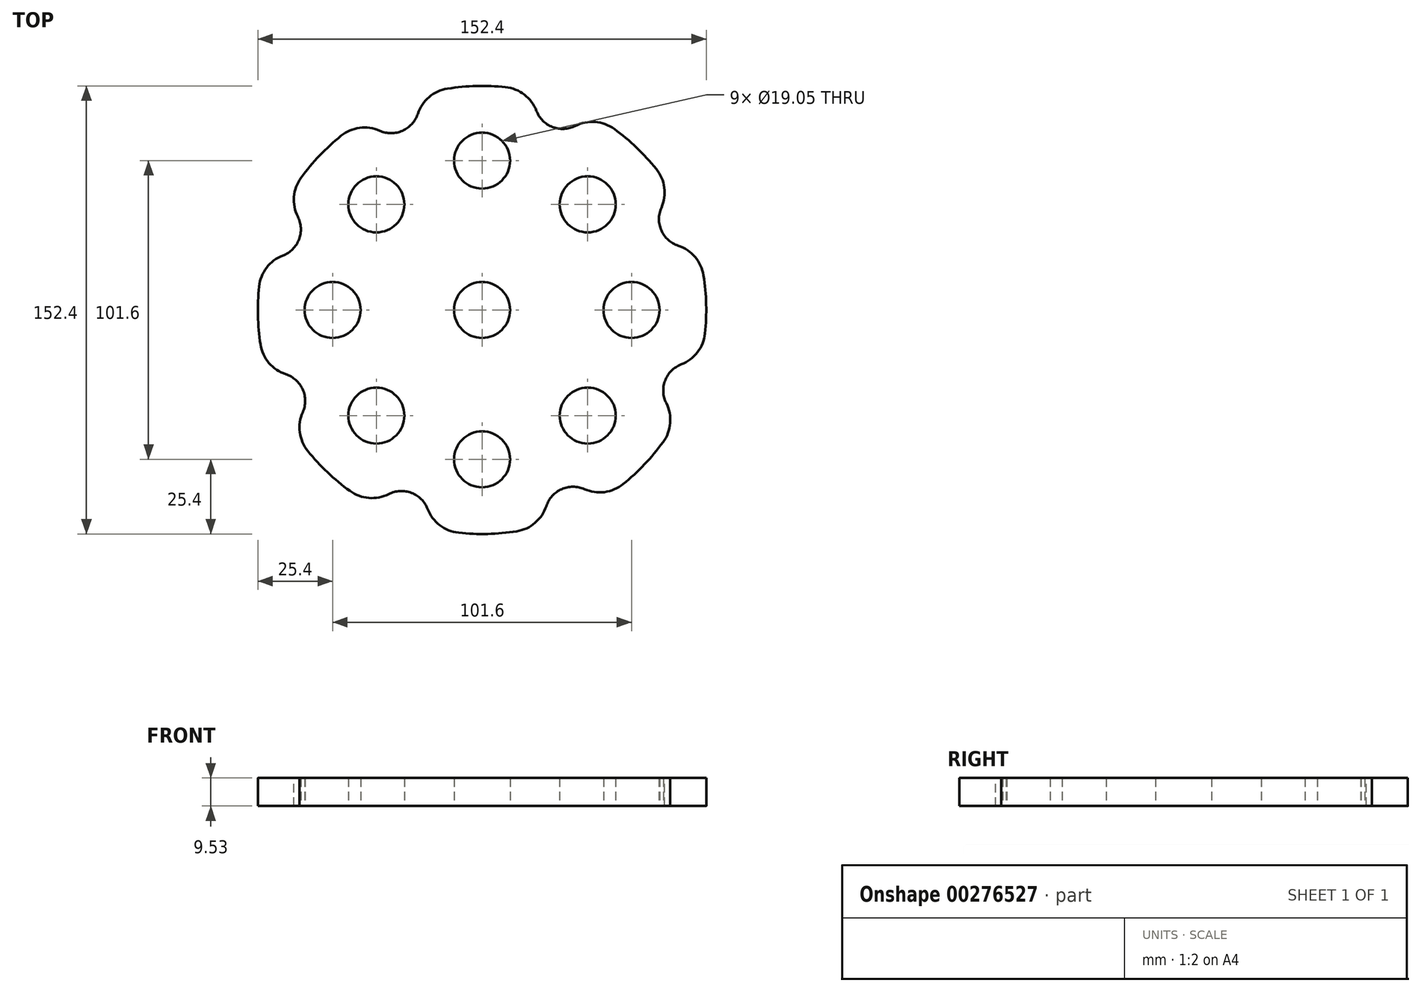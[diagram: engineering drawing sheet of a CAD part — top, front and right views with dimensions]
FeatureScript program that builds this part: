
annotation { "Feature Type Name" : "Feature", "Feature Type Description" : "" }
export const myFeature = defineFeature(function(context is Context, id is Id, definition is map)
    precondition{}
    {
        {
            var Q0;
            Q0=qCreatedBy(makeId("Top.planeOp"),FACE);
            var sketch = newSketch(context, id + "F0", { "sketchPlane" : qUnion([Q0])});
            skCircle(sketch, "E0", {"center": v(0, 0) * mm, "radius": 9.53 * mm});
            skCircle(sketch, "E1", {"center": v(0, 50.8) * mm, "radius": 9.53 * mm});
            skArc(sketch, "E2", {"start": v(-73.97, 18.31) * mm, "mid": v(-76.18, -1.9) * mm, "end": v(-72.96, -21.97) * mm});
            skCircle(sketch, "E3.1.0", {"center": v(-35.92, 35.92) * mm, "radius": 9.53 * mm});
            skCircle(sketch, "E3.2.0", {"center": v(-50.8, 0) * mm, "radius": 9.53 * mm});
            skCircle(sketch, "E3.3.0", {"center": v(-35.92, -35.92) * mm, "radius": 9.53 * mm});
            skCircle(sketch, "E3.4.0", {"center": v(0, -50.8) * mm, "radius": 9.53 * mm});
            skCircle(sketch, "E3.5.0", {"center": v(35.92, -35.92) * mm, "radius": 9.53 * mm});
            skCircle(sketch, "E3.6.0", {"center": v(50.8, 0) * mm, "radius": 9.53 * mm});
            skCircle(sketch, "E3.7.0", {"center": v(35.92, 35.92) * mm, "radius": 9.53 * mm});
            skArc(sketch, "E4", {"start": v(-39.35, 65.25) * mm, "mid": v(-27.04, 60.95) * mm, "end": v(-21.97, 72.96) * mm});
            skArc(sketch, "E5.1.0", {"start": v(-73.97, 18.31) * mm, "mid": v(-62.22, 23.97) * mm, "end": v(-67.13, 36.05) * mm});
            skArc(sketch, "E5.2.0", {"start": v(-65.25, -39.35) * mm, "mid": v(-60.95, -27.04) * mm, "end": v(-72.96, -21.97) * mm});
            skArc(sketch, "E5.3.0", {"start": v(-18.31, -73.97) * mm, "mid": v(-23.97, -62.22) * mm, "end": v(-36.05, -67.13) * mm});
            skArc(sketch, "E5.4.0", {"start": v(39.35, -65.25) * mm, "mid": v(27.04, -60.95) * mm, "end": v(21.97, -72.96) * mm});
            skArc(sketch, "E5.5.0", {"start": v(73.97, -18.31) * mm, "mid": v(62.22, -23.97) * mm, "end": v(67.13, -36.05) * mm});
            skArc(sketch, "E5.6.0", {"start": v(65.25, 39.35) * mm, "mid": v(60.95, 27.04) * mm, "end": v(72.96, 21.97) * mm});
            skArc(sketch, "E5.7.0", {"start": v(18.31, 73.97) * mm, "mid": v(23.97, 62.22) * mm, "end": v(36.05, 67.13) * mm});
            skArc(sketch, "E6.trimOffspring", {"start": v(-39.35, 65.25) * mm, "mid": v(-55.2, 52.52) * mm, "end": v(-67.13, 36.05) * mm});
            skArc(sketch, "E7.trimOffspring", {"start": v(65.25, 39.35) * mm, "mid": v(52.52, 55.2) * mm, "end": v(36.05, 67.13) * mm});
            skArc(sketch, "E8.trimOffspring", {"start": v(18.31, 73.97) * mm, "mid": v(-1.9, 76.18) * mm, "end": v(-21.97, 72.96) * mm});
            skArc(sketch, "E9.trimOffspring", {"start": v(73.97, -18.31) * mm, "mid": v(76.18, 1.9) * mm, "end": v(72.96, 21.97) * mm});
            skArc(sketch, "E10.trimOffspring", {"start": v(39.35, -65.25) * mm, "mid": v(55.2, -52.52) * mm, "end": v(67.13, -36.05) * mm});
            skArc(sketch, "E11.trimOffspring", {"start": v(-18.31, -73.97) * mm, "mid": v(1.9, -76.18) * mm, "end": v(21.97, -72.96) * mm});
            skArc(sketch, "E12.trimOffspring", {"start": v(-65.25, -39.35) * mm, "mid": v(-52.52, -55.2) * mm, "end": v(-36.05, -67.13) * mm});
            skSolve(sketch);
        }
        {
            var Q0;
            Q0 = qSketchRegion(id + "F0", true);
            extrude(context, id + "F1", {"entities" : qUnion([Q0]), "depth" : 9.52 * mm});
        }
        {
            var Q0;
            Q0=makeQuery(id+"F1.opExtrude","SWEPT_EDGE",EDGE,{"disambiguationData":[OSD([sQuery(id+"F0.wireOp",EDGE,"E4"),sQuery(id+"F0.wireOp",EDGE,"E8.trimOffspring")])]});
            var Q1;
            Q1=makeQuery(id+"F1.opExtrude","SWEPT_EDGE",EDGE,{"disambiguationData":[OSD([sQuery(id+"F0.wireOp",EDGE,"E4"),sQuery(id+"F0.wireOp",EDGE,"E6.trimOffspring")])]});
            var Q2;
            Q2=makeQuery(id+"F1.opExtrude","SWEPT_EDGE",EDGE,{"disambiguationData":[OSD([sQuery(id+"F0.wireOp",EDGE,"E5.1.0"),sQuery(id+"F0.wireOp",EDGE,"E6.trimOffspring")])]});
            var Q3;
            Q3=makeQuery(id+"F1.opExtrude","SWEPT_EDGE",EDGE,{"disambiguationData":[OSD([sQuery(id+"F0.wireOp",EDGE,"E2"),sQuery(id+"F0.wireOp",EDGE,"E5.1.0")])]});
            var Q4;
            Q4=makeQuery(id+"F1.opExtrude","SWEPT_EDGE",EDGE,{"disambiguationData":[OSD([sQuery(id+"F0.wireOp",EDGE,"E2"),sQuery(id+"F0.wireOp",EDGE,"E5.2.0")])]});
            var Q5;
            Q5=makeQuery(id+"F1.opExtrude","SWEPT_EDGE",EDGE,{"disambiguationData":[OSD([sQuery(id+"F0.wireOp",EDGE,"E5.2.0"),sQuery(id+"F0.wireOp",EDGE,"E12.trimOffspring")])]});
            var Q6;
            Q6=makeQuery(id+"F1.opExtrude","SWEPT_EDGE",EDGE,{"disambiguationData":[OSD([sQuery(id+"F0.wireOp",EDGE,"E5.3.0"),sQuery(id+"F0.wireOp",EDGE,"E12.trimOffspring")])]});
            var Q7;
            Q7=makeQuery(id+"F1.opExtrude","SWEPT_EDGE",EDGE,{"disambiguationData":[OSD([sQuery(id+"F0.wireOp",EDGE,"E5.3.0"),sQuery(id+"F0.wireOp",EDGE,"E11.trimOffspring")])]});
            var Q8;
            Q8=makeQuery(id+"F1.opExtrude","SWEPT_EDGE",EDGE,{"disambiguationData":[OSD([sQuery(id+"F0.wireOp",EDGE,"E5.4.0"),sQuery(id+"F0.wireOp",EDGE,"E10.trimOffspring")])]});
            var Q9;
            Q9=makeQuery(id+"F1.opExtrude","SWEPT_EDGE",EDGE,{"disambiguationData":[OSD([sQuery(id+"F0.wireOp",EDGE,"E5.4.0"),sQuery(id+"F0.wireOp",EDGE,"E11.trimOffspring")])]});
            var Q10;
            Q10=makeQuery(id+"F1.opExtrude","SWEPT_EDGE",EDGE,{"disambiguationData":[OSD([sQuery(id+"F0.wireOp",EDGE,"E5.5.0"),sQuery(id+"F0.wireOp",EDGE,"E9.trimOffspring")])]});
            var Q11;
            Q11=makeQuery(id+"F1.opExtrude","SWEPT_EDGE",EDGE,{"disambiguationData":[OSD([sQuery(id+"F0.wireOp",EDGE,"E5.5.0"),sQuery(id+"F0.wireOp",EDGE,"E10.trimOffspring")])]});
            var Q12;
            Q12=makeQuery(id+"F1.opExtrude","SWEPT_EDGE",EDGE,{"disambiguationData":[OSD([sQuery(id+"F0.wireOp",EDGE,"E5.6.0"),sQuery(id+"F0.wireOp",EDGE,"E9.trimOffspring")])]});
            var Q13;
            Q13=makeQuery(id+"F1.opExtrude","SWEPT_EDGE",EDGE,{"disambiguationData":[OSD([sQuery(id+"F0.wireOp",EDGE,"E5.6.0"),sQuery(id+"F0.wireOp",EDGE,"E7.trimOffspring")])]});
            var Q14;
            Q14=makeQuery(id+"F1.opExtrude","SWEPT_EDGE",EDGE,{"disambiguationData":[OSD([sQuery(id+"F0.wireOp",EDGE,"E5.7.0"),sQuery(id+"F0.wireOp",EDGE,"E8.trimOffspring")])]});
            var Q15;
            Q15=makeQuery(id+"F1.opExtrude","SWEPT_EDGE",EDGE,{"disambiguationData":[OSD([sQuery(id+"F0.wireOp",EDGE,"E5.7.0"),sQuery(id+"F0.wireOp",EDGE,"E7.trimOffspring")])]});
            fillet(context, id + "F2", {"entities" : qUnion([Q0, Q1, Q2, Q3, Q4, Q5, Q6, Q7, Q8, Q9, Q10, Q11, Q12, Q13, Q14, Q15]), "radius" : 12.7 * mm, "tangentPropagation" : true, "allowEdgeOverflow" : false});
        }
    });
